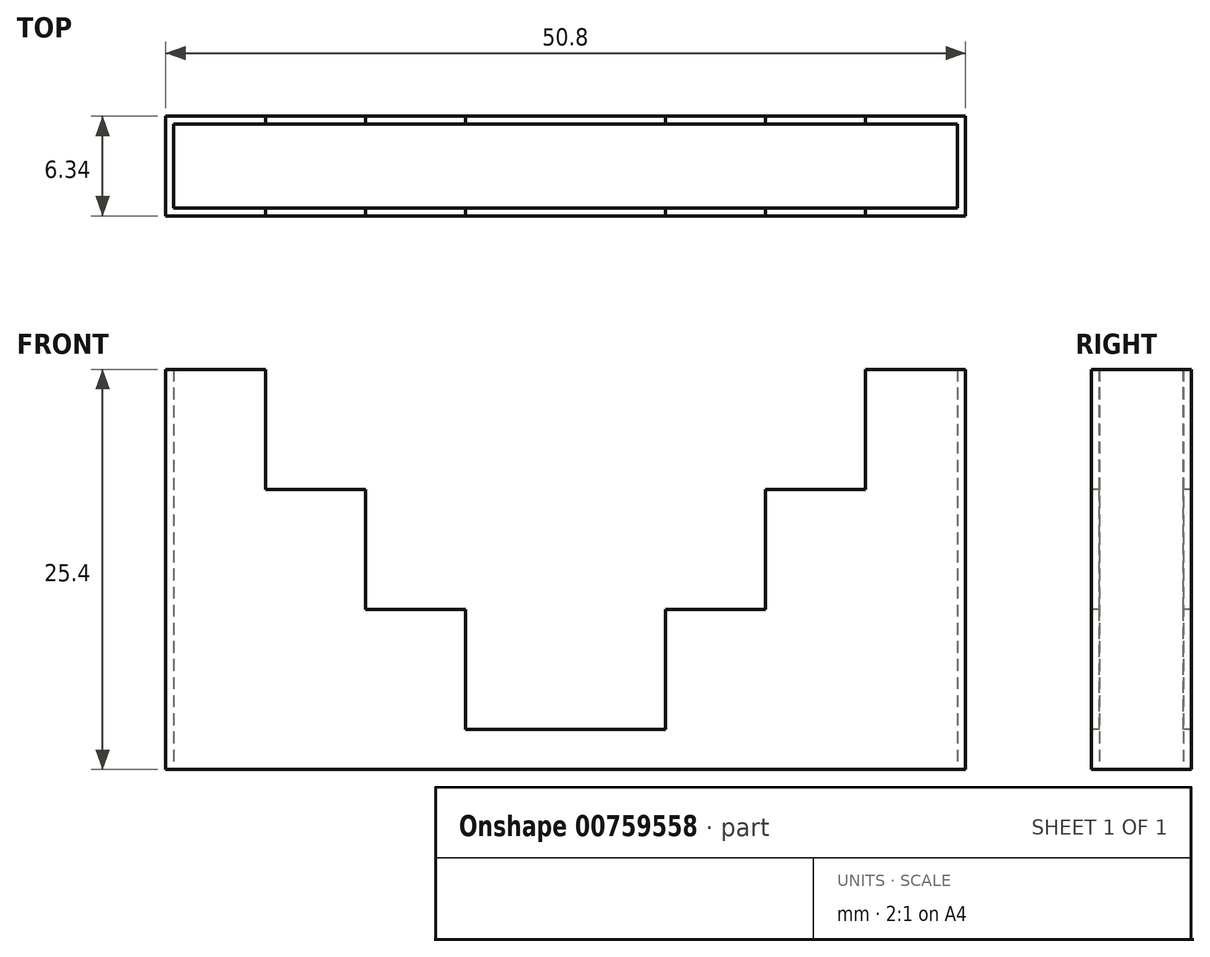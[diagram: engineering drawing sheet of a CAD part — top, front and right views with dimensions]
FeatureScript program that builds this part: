
annotation { "Feature Type Name" : "Feature", "Feature Type Description" : "" }
export const myFeature = defineFeature(function(context is Context, id is Id, definition is map)
    precondition{}
    {
        {
            var Q0;
            Q0=qCreatedBy(makeId("Top.planeOp"),FACE);
            var sketch = newSketch(context, id + "F0", { "sketchPlane" : qUnion([Q0])});
            skLineSegment(sketch, "E0.bottom", {"start": v(-25.4, -3.18) * mm, "end": v(25.4, -3.18) * mm});
            skLineSegment(sketch, "E0.top", {"start": v(-25.4, 3.18) * mm, "end": v(25.4, 3.18) * mm});
            skLineSegment(sketch, "E0.left", {"start": v(-25.4, -3.18) * mm, "end": v(-25.4, 3.18) * mm});
            skLineSegment(sketch, "E0.right", {"start": v(25.4, -3.18) * mm, "end": v(25.4, 3.18) * mm});
            skPoint(sketch, "E0.middle", {"position": v(0, 0) * mm});
            skSolve(sketch);
        }
        {
            var Q0;
            Q0=qSketchRegion(id+"F0",true);
            extrude(context, id + "F1", {"entities" : qUnion([Q0]), "depth" : 25.4 * mm, "offsetDistance" : 25.4 * mm});
        }
        {
            var Q0;
            Q0=makeQuery(id+"F1.opExtrude","CAP_FACE",FACE,{"disambiguationData":[OSD([sQuery(id+"F0.wireOp",EDGE,"E0.bottom"),sQuery(id+"F0.wireOp",EDGE,"E0.top"),sQuery(id+"F0.wireOp",EDGE,"E0.left"),sQuery(id+"F0.wireOp",EDGE,"E0.right")])],"isStart":false});
            var Q1;
            Q1=makeQuery(id+"F1.opExtrude","CAP_FACE",FACE,{"disambiguationData":[OSD([sQuery(id+"F0.wireOp",EDGE,"E0.bottom"),sQuery(id+"F0.wireOp",EDGE,"E0.top"),sQuery(id+"F0.wireOp",EDGE,"E0.left"),sQuery(id+"F0.wireOp",EDGE,"E0.right")])],"isStart":true});
            shell(context, id + "F2", {"entities" : qUnion([Q0, Q1]), "thickness" : 0.5 * mm});
        }
        {
            var Q0;
            Q0=makeQuery(id+"F1.opExtrude","SWEPT_FACE",FACE,{"disambiguationData":[OSD([sQuery(id+"F0.wireOp",EDGE,"E0.bottom")])]});
            var sketch = newSketch(context, id + "F3", { "sketchPlane" : qUnion([Q0])});
            skLineSegment(sketch, "E1.bottom", {"start": v(-19.05, 25.4) * mm, "end": v(19.05, 25.4) * mm});
            skLineSegment(sketch, "E1.top", {"start": v(-19.05, 17.78) * mm, "end": v(19.05, 17.78) * mm});
            skLineSegment(sketch, "E1.left", {"start": v(-19.05, 25.4) * mm, "end": v(-19.05, 17.78) * mm});
            skLineSegment(sketch, "E1.right", {"start": v(19.05, 25.4) * mm, "end": v(19.05, 17.78) * mm});
            skLineSegment(sketch, "E2.bottom", {"start": v(-12.7, 25.4) * mm, "end": v(12.7, 25.4) * mm});
            skLineSegment(sketch, "E2.top", {"start": v(-12.7, 10.16) * mm, "end": v(12.7, 10.16) * mm});
            skLineSegment(sketch, "E2.left", {"start": v(-12.7, 25.4) * mm, "end": v(-12.7, 10.16) * mm});
            skLineSegment(sketch, "E2.right", {"start": v(12.7, 25.4) * mm, "end": v(12.7, 10.16) * mm});
            skLineSegment(sketch, "E3.bottom", {"start": v(-6.35, 25.4) * mm, "end": v(6.35, 25.4) * mm});
            skLineSegment(sketch, "E3.top", {"start": v(-6.35, 2.54) * mm, "end": v(6.35, 2.54) * mm});
            skLineSegment(sketch, "E3.left", {"start": v(-6.35, 25.4) * mm, "end": v(-6.35, 2.54) * mm});
            skLineSegment(sketch, "E3.right", {"start": v(6.35, 25.4) * mm, "end": v(6.35, 2.54) * mm});
            skSolve(sketch);
        }
        {
            var Q0;
            Q0=qSketchRegion(id+"F3",true);
            extrude(context, id + "F4", {"entities" : qUnion([Q0]), "operationType" : NewBodyOperationType.REMOVE, "oppositeDirection" : true, "depth" : 13.2 * mm, "offsetDistance" : 25.4 * mm});
        }
    });
